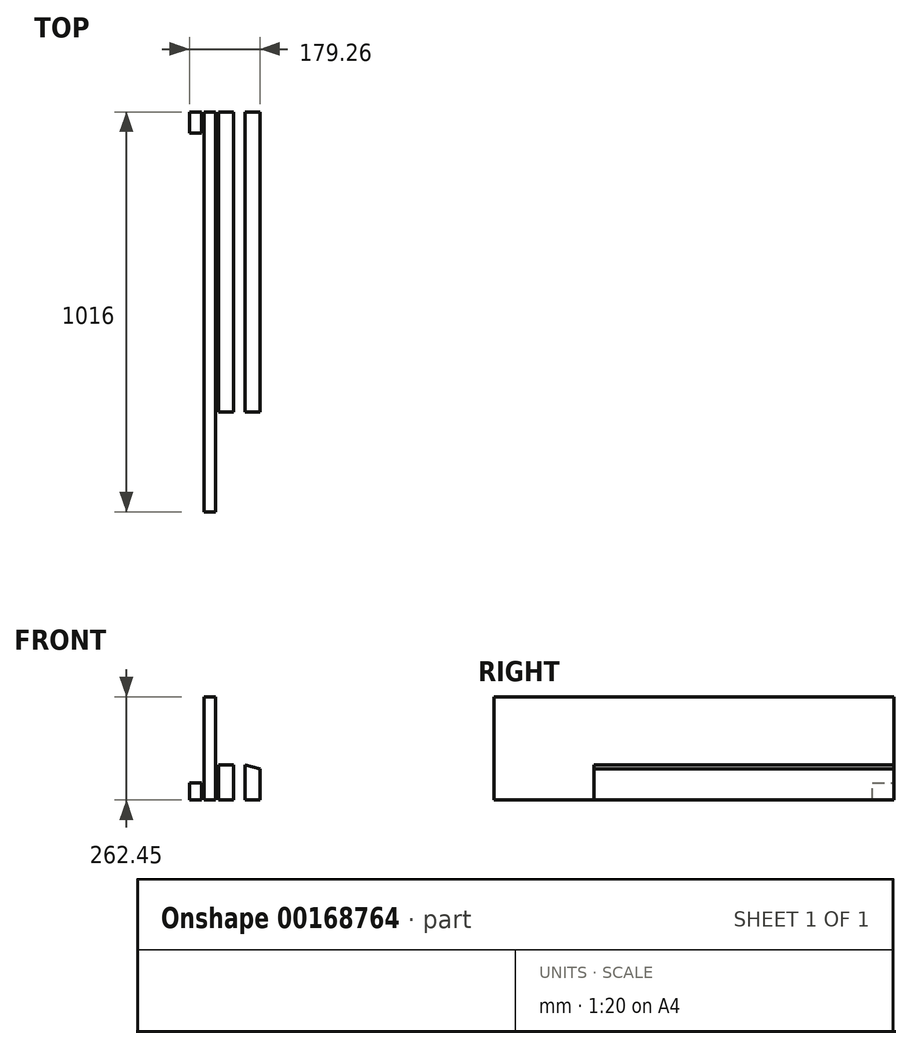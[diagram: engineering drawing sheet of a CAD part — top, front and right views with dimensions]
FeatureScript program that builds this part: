
annotation { "Feature Type Name" : "Feature", "Feature Type Description" : "" }
export const myFeature = defineFeature(function(context is Context, id is Id, definition is map)
    precondition{}
    {
        {
            var Q0;
            Q0=qCreatedBy(makeId("Front.planeOp"),FACE);
            var sketch = newSketch(context, id + "F0", { "sketchPlane" : qUnion([Q0])});
            skLineSegment(sketch, "E0.bottom", {"start": v(0, 0) * mm, "end": v(38.1, 0) * mm});
            skLineSegment(sketch, "E0.top", {"start": v(0, 88.9) * mm, "end": v(38.1, 88.9) * mm});
            skLineSegment(sketch, "E0.left", {"start": v(0, 0) * mm, "end": v(0, 88.9) * mm});
            skLineSegment(sketch, "E0.right", {"start": v(38.1, 0) * mm, "end": v(38.1, 88.9) * mm});
            skSolve(sketch);
        }
        {
            var Q0;
            Q0=makeQuery(id+"F0.imprint","IMPRINT",FACE,{"disambiguationData":[TD([[makeQuery(id+"F0.imprint","IMPRINT",EDGE,{"derivedFrom":sQuery(id+"F0.wireOp",EDGE,"E0.bottom")}),1.0]])]});
            extrude(context, id + "F1", {"entities" : qUnion([Q0]), "depth" : 762 * mm});
        }
        {
            var Q0;
            Q0=qCreatedBy(makeId("Front.planeOp"),FACE);
            var sketch = newSketch(context, id + "F2", { "sketchPlane" : qUnion([Q0])});
            skLineSegment(sketch, "E1.bottom", {"start": v(-73.76, 0) * mm, "end": v(-43.28, 0) * mm});
            skLineSegment(sketch, "E1.top", {"start": v(-73.76, 43.18) * mm, "end": v(-43.28, 43.18) * mm});
            skLineSegment(sketch, "E1.left", {"start": v(-73.76, 0) * mm, "end": v(-73.76, 43.18) * mm});
            skLineSegment(sketch, "E1.right", {"start": v(-43.28, 0) * mm, "end": v(-43.28, 43.18) * mm});
            skSolve(sketch);
        }
        {
            var Q0;
            Q0=makeQuery(id+"F2.imprint","IMPRINT",FACE,{"disambiguationData":[TD([[makeQuery(id+"F2.imprint","IMPRINT",EDGE,{"derivedFrom":sQuery(id+"F2.wireOp",EDGE,"E1.bottom")}),1.0]])]});
            extrude(context, id + "F3", {"entities" : qUnion([Q0]), "depth" : 54.36 * mm});
        }
        {
            var Q0;
            Q0=qCreatedBy(makeId("Front.planeOp"),FACE);
            var sketch = newSketch(context, id + "F4", { "sketchPlane" : qUnion([Q0])});
            skLineSegment(sketch, "E2.bottom", {"start": v(67.4, 0) * mm, "end": v(105.5, 0) * mm});
            skLineSegment(sketch, "E2.left", {"start": v(67.4, 0) * mm, "end": v(67.4, 88.9) * mm});
            skLineSegment(sketch, "E2.right", {"start": v(105.5, 0) * mm, "end": v(105.5, 78.96) * mm});
            skLineSegment(sketch, "E3", {"start": v(67.4, 88.9) * mm, "end": v(105.5, 78.96) * mm});
            skSolve(sketch);
        }
        {
            var Q0;
            Q0=makeQuery(id+"F4.imprint","IMPRINT",FACE,{"disambiguationData":[TD([[makeQuery(id+"F4.imprint","IMPRINT",EDGE,{"derivedFrom":sQuery(id+"F4.wireOp",EDGE,"E2.bottom")}),1.0]])]});
            extrude(context, id + "F5", {"entities" : qUnion([Q0]), "depth" : 762 * mm});
        }
        {
            var Q0;
            Q0=qCreatedBy(makeId("Front.planeOp"),FACE);
            var sketch = newSketch(context, id + "F6", { "sketchPlane" : qUnion([Q0])});
            skLineSegment(sketch, "E4.bottom", {"start": v(-37.02, 0) * mm, "end": v(-7.2, 0) * mm});
            skLineSegment(sketch, "E4.top", {"start": v(-37.02, 262.45) * mm, "end": v(-7.2, 262.45) * mm});
            skLineSegment(sketch, "E4.left", {"start": v(-37.02, 0) * mm, "end": v(-37.02, 262.45) * mm});
            skLineSegment(sketch, "E4.right", {"start": v(-7.2, 0) * mm, "end": v(-7.2, 262.45) * mm});
            skSolve(sketch);
        }
        {
            var Q0;
            Q0=makeQuery(id+"F6.imprint","IMPRINT",FACE,{"disambiguationData":[TD([[makeQuery(id+"F6.imprint","IMPRINT",EDGE,{"derivedFrom":sQuery(id+"F6.wireOp",EDGE,"E4.bottom")}),1.0]])]});
            extrude(context, id + "F7", {"entities" : qUnion([Q0]), "depth" : 1016 * mm});
        }
    });
